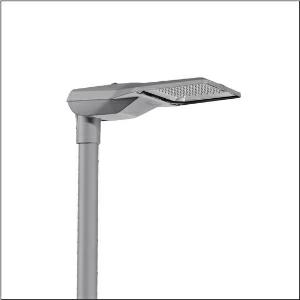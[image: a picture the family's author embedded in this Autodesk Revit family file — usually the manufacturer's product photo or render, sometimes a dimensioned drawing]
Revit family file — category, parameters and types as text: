
# Revit family: streetlight_sl_21_midi___st0_8a_5xe3c33s08nb_db16
name_source: partatom
category: Lighting Fixtures
units: mm (PartAtom-declared; Revit-internal decimal feet)

## family parameters
Cut with Voids When Loaded = No
Host = Face
Light Source = No
Part Type = Normal
Room Calculation Point = No
Round Connector Dimension = Use Diameter
Shared = No

## types (1)
- --- (1 x LED, 22700 lm, 151.2 W, 3000K)
    Apparent Load = 151 VA
    CIE Flux Codes = 41 75 97 100 100
    Color Rendering = 70
    Color Temperature = 3000K
    Default Elevation = 1800 mm
    Description = Streetlight SL 21 midi, mast luminaire, primary light control with lens, of PMMA, primary optical cover: cover, of toughened safety glass, transparent, light distribution: ST0.8a, light emission: direct distribution, primary light characteristic: asymmetric, installation type: side-entry, post-top, LED, High Power LED, rated luminous flux: 22.700lm, luminous efficacy: 150lm/W, light colour: 730, colour temperature: 3000K, control: overheat protection, constant luminous flux control, time-dependent luminous flux control, flexible luminous flux parameterisation, presetting dimming logarithmic, mains connection: 230..240V, AC, 50/60Hz, start of lifetime: 151W, end of service life: 157W, reduction: 70W, luminaire housing, of diecast aluminium, powder-coated, Siteco® metallic grey (DB 702S), corrosivity category C5 mid according to DIN EN ISO 12944, please order mast flange separately, inclination adjustable: 0°, 5°, 10°, 15°, sealing non-destructively replaceable, multi-level sealing system, length: 644mm, width: 335mm, height: 110mm, mast flange for spigot size: 42mm (side-entry): 5XC10008XM4, 60/48mm (side-entry/post-top): 5XC10108XM2, 76/60mm (side-entry/post-top): 5XC10108XM1, Smart Interface above, protection rating (complete): IP66, insulation class (complete): insulation class II (safety insulation), certification: CE, ENEC, ENEC+, VDE, impact resistance: IK09, permissible operating ambient temperature for outdoor applications: -40..+50°C, standard-compliant lighting for roads and squares, packaging unit: 1 piece

Light Distribution: ST0.8a
    Height = 111 mm
    Lamp = 1 x LED
    Lamp Light Flux = 22700 lm
    Lamp Power = 151.2 W
    Lamp count = 1
    Length = 644 mm
    Luminous efficacy = 150 lm/W
    Manufacturer = Siteco
    ModVariant = No
    Model = 5XE3C33S08NB
    Number of Poles = 1
    OnlyDefault = Yes
    Power Factor = 1
    Product Name = Streetlight SL 21 midi | ST0.8a
    Product group = mast luminaire | pylon top
    ProductGroupID = 6100
    Protection Class = Protection class II
    Protection Degree = IP 66
    RLX_Detail_Level = 1
    RLX_Emergency_Light_Flux = 0 lm
    RLX_Emergency_Type = 0
    RLX_Emergency_Type_DB = No
    RlxData = <blob elided: 91821 chars, md5=b88a32eb>
    Socket = socket
    Standby Power = 0 W
    System Light Flux = 22700 lm
    System Power = 151 W
    Type Comments = factory setting: luminous flux: 100 % | dim-lin: 254 | 802 mA
    Type Image = l_1004302.jpg
    URL = http://relux.com
    VarID = @adj_119039
    Voltage = 0 V
    Weight = 0.00 kg
    Width = 336 mm

## geometry (parser evidence)
native form markers: Blend x4, Sweep x11
no freeform markers — native parametric forms only
